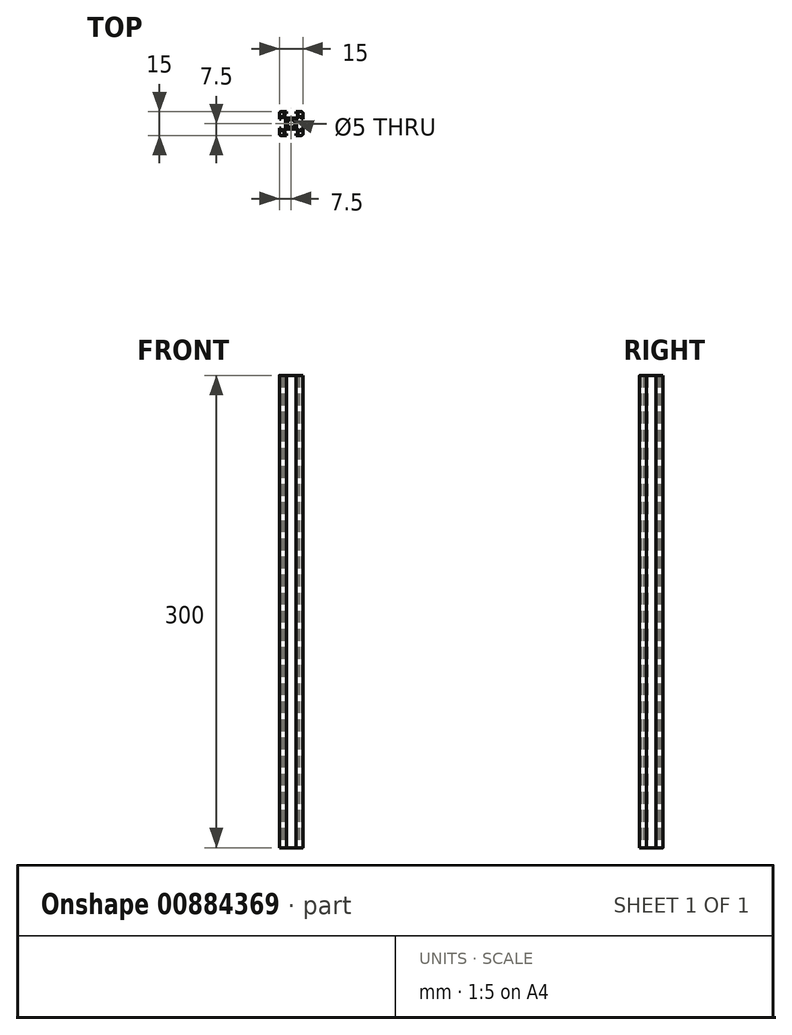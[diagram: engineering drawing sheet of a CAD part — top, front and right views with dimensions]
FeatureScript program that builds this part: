
annotation { "Feature Type Name" : "Feature", "Feature Type Description" : "" }
export const myFeature = defineFeature(function(context is Context, id is Id, definition is map)
    precondition{}
    {
        {
            var Q0;
            Q0=qCreatedBy(makeId("Top.planeOp"),FACE);
            var sketch = newSketch(context, id + "F0", { "sketchPlane" : qUnion([Q0])});
            skCircle(sketch, "E0", {"center": v(0, 0) * mm, "radius": 2.5 * mm});
            skLineSegment(sketch, "E1.bottom", {"start": v(6.5, 7.5) * mm, "end": v(3, 7.5) * mm});
            skLineSegment(sketch, "E1.top", {"start": v(6.5, -7.5) * mm, "end": v(3, -7.5) * mm});
            skLineSegment(sketch, "E1.left", {"start": v(7.5, 6.5) * mm, "end": v(7.5, 3) * mm});
            skLineSegment(sketch, "E1.right", {"start": v(-7.5, 6.5) * mm, "end": v(-7.5, 3) * mm});
            skPoint(sketch, "E2.visualSharp", {"position": v(-7.5, 7.5) * mm});
            skArc(sketch, "E2.filletArc", {"start": v(-6.5, 7.5) * mm, "mid": v(-7.2, 7.2) * mm, "end": v(-7.5, 6.5) * mm});
            skPoint(sketch, "E3.visualSharp", {"position": v(7.5, 7.5) * mm});
            skArc(sketch, "E3.filletArc", {"start": v(7.5, 6.5) * mm, "mid": v(7.2, 7.2) * mm, "end": v(6.5, 7.5) * mm});
            skPoint(sketch, "E4.visualSharp", {"position": v(7.5, -7.5) * mm});
            skArc(sketch, "E4.filletArc", {"start": v(6.5, -7.5) * mm, "mid": v(7.2, -7.2) * mm, "end": v(7.5, -6.5) * mm});
            skPoint(sketch, "E5.visualSharp", {"position": v(-7.5, -7.5) * mm});
            skArc(sketch, "E5.filletArc", {"start": v(-7.5, -6.5) * mm, "mid": v(-7.2, -7.2) * mm, "end": v(-6.5, -7.5) * mm});
            skLineSegment(sketch, "E6", {"start": v(-3, 7.5) * mm, "end": v(-3, 6.5) * mm});
            skLineSegment(sketch, "E7", {"start": v(3, 7.5) * mm, "end": v(3, 6.5) * mm});
            skLineSegment(sketch, "E8", {"start": v(-4.5, 6.5) * mm, "end": v(-4.5, 5) * mm});
            skLineSegment(sketch, "E9", {"start": v(4.5, 5) * mm, "end": v(4.5, 6.5) * mm});
            skLineSegment(sketch, "E10", {"start": v(4.5, 6.5) * mm, "end": v(3, 6.5) * mm});
            skLineSegment(sketch, "E11", {"start": v(-3, 3.5) * mm, "end": v(3, 3.5) * mm});
            skLineSegment(sketch, "E12", {"start": v(3, 3.5) * mm, "end": v(4.5, 5) * mm});
            skLineSegment(sketch, "E13", {"start": v(-3, 3.5) * mm, "end": v(-4.5, 5) * mm});
            skLineSegment(sketch, "E14.trimOffspring", {"start": v(-3, 6.5) * mm, "end": v(-4.5, 6.5) * mm});
            skLineSegment(sketch, "E15", {"start": v(-3, -7.5) * mm, "end": v(-3, -6.5) * mm});
            skLineSegment(sketch, "E16", {"start": v(-3, -6.5) * mm, "end": v(-4.5, -6.5) * mm});
            skLineSegment(sketch, "E17", {"start": v(-4.5, -6.5) * mm, "end": v(-4.5, -5) * mm});
            skLineSegment(sketch, "E18", {"start": v(-4.5, -5) * mm, "end": v(-3, -3.5) * mm});
            skLineSegment(sketch, "E19", {"start": v(-3, -3.5) * mm, "end": v(3, -3.5) * mm});
            skLineSegment(sketch, "E20", {"start": v(3, -3.5) * mm, "end": v(4.5, -5) * mm});
            skLineSegment(sketch, "E21", {"start": v(4.5, -5) * mm, "end": v(4.5, -6.5) * mm});
            skLineSegment(sketch, "E22", {"start": v(4.5, -6.5) * mm, "end": v(3, -6.5) * mm});
            skLineSegment(sketch, "E23", {"start": v(3, -6.5) * mm, "end": v(3, -7.5) * mm});
            skPoint(sketch, "E24", {"position": v(0, 7.5) * mm});
            skPoint(sketch, "E25", {"position": v(0, -7.5) * mm});
            skPoint(sketch, "E26", {"position": v(7.5, 0) * mm});
            skPoint(sketch, "E27", {"position": v(-7.5, 0) * mm});
            skLineSegment(sketch, "E28", {"start": v(7.5, 3) * mm, "end": v(6.5, 3) * mm});
            skLineSegment(sketch, "E29", {"start": v(6.5, 3) * mm, "end": v(6.5, 4.5) * mm});
            skLineSegment(sketch, "E30", {"start": v(6.5, 4.5) * mm, "end": v(5, 4.5) * mm});
            skLineSegment(sketch, "E31", {"start": v(5, 4.5) * mm, "end": v(3.5, 3) * mm});
            skLineSegment(sketch, "E32", {"start": v(3.5, 3) * mm, "end": v(3.5, -3) * mm});
            skLineSegment(sketch, "E33", {"start": v(3.5, -3) * mm, "end": v(5, -4.5) * mm});
            skLineSegment(sketch, "E34", {"start": v(5, -4.5) * mm, "end": v(6.5, -4.5) * mm});
            skLineSegment(sketch, "E35", {"start": v(6.5, -4.5) * mm, "end": v(6.5, -3) * mm});
            skLineSegment(sketch, "E36", {"start": v(6.5, -3) * mm, "end": v(7.5, -3) * mm});
            skLineSegment(sketch, "E37.trimOffspring", {"start": v(-3, 7.5) * mm, "end": v(-6.5, 7.5) * mm});
            skLineSegment(sketch, "E38.trimOffspring", {"start": v(7.5, -3) * mm, "end": v(7.5, -6.5) * mm});
            skLineSegment(sketch, "E39.trimOffspring", {"start": v(-3, -7.5) * mm, "end": v(-6.5, -7.5) * mm});
            skLineSegment(sketch, "E40", {"start": v(-7.5, 3) * mm, "end": v(-6.5, 3) * mm});
            skLineSegment(sketch, "E41", {"start": v(-6.5, 3) * mm, "end": v(-6.5, 4.5) * mm});
            skLineSegment(sketch, "E42", {"start": v(-6.5, 4.5) * mm, "end": v(-5, 4.5) * mm});
            skLineSegment(sketch, "E43", {"start": v(-5, 4.5) * mm, "end": v(-3.5, 3) * mm});
            skLineSegment(sketch, "E44", {"start": v(-3.5, 3) * mm, "end": v(-3.5, -3) * mm});
            skLineSegment(sketch, "E45", {"start": v(-3.5, -3) * mm, "end": v(-5, -4.5) * mm});
            skLineSegment(sketch, "E46", {"start": v(-5, -4.5) * mm, "end": v(-6.5, -4.5) * mm});
            skLineSegment(sketch, "E47", {"start": v(-6.5, -4.5) * mm, "end": v(-6.5, -3) * mm});
            skLineSegment(sketch, "E48", {"start": v(-6.5, -3) * mm, "end": v(-7.5, -3) * mm});
            skLineSegment(sketch, "E49.trimOffspring", {"start": v(-7.5, -3) * mm, "end": v(-7.5, -6.5) * mm});
            skSolve(sketch);
        }
        {
            var Q0;
            Q0=qSketchRegion(id+"F0",true);
            extrude(context, id + "F1", {"entities" : qUnion([Q0]), "depth" : 300 * mm, "offsetDistance" : 25 * mm});
        }
    });
